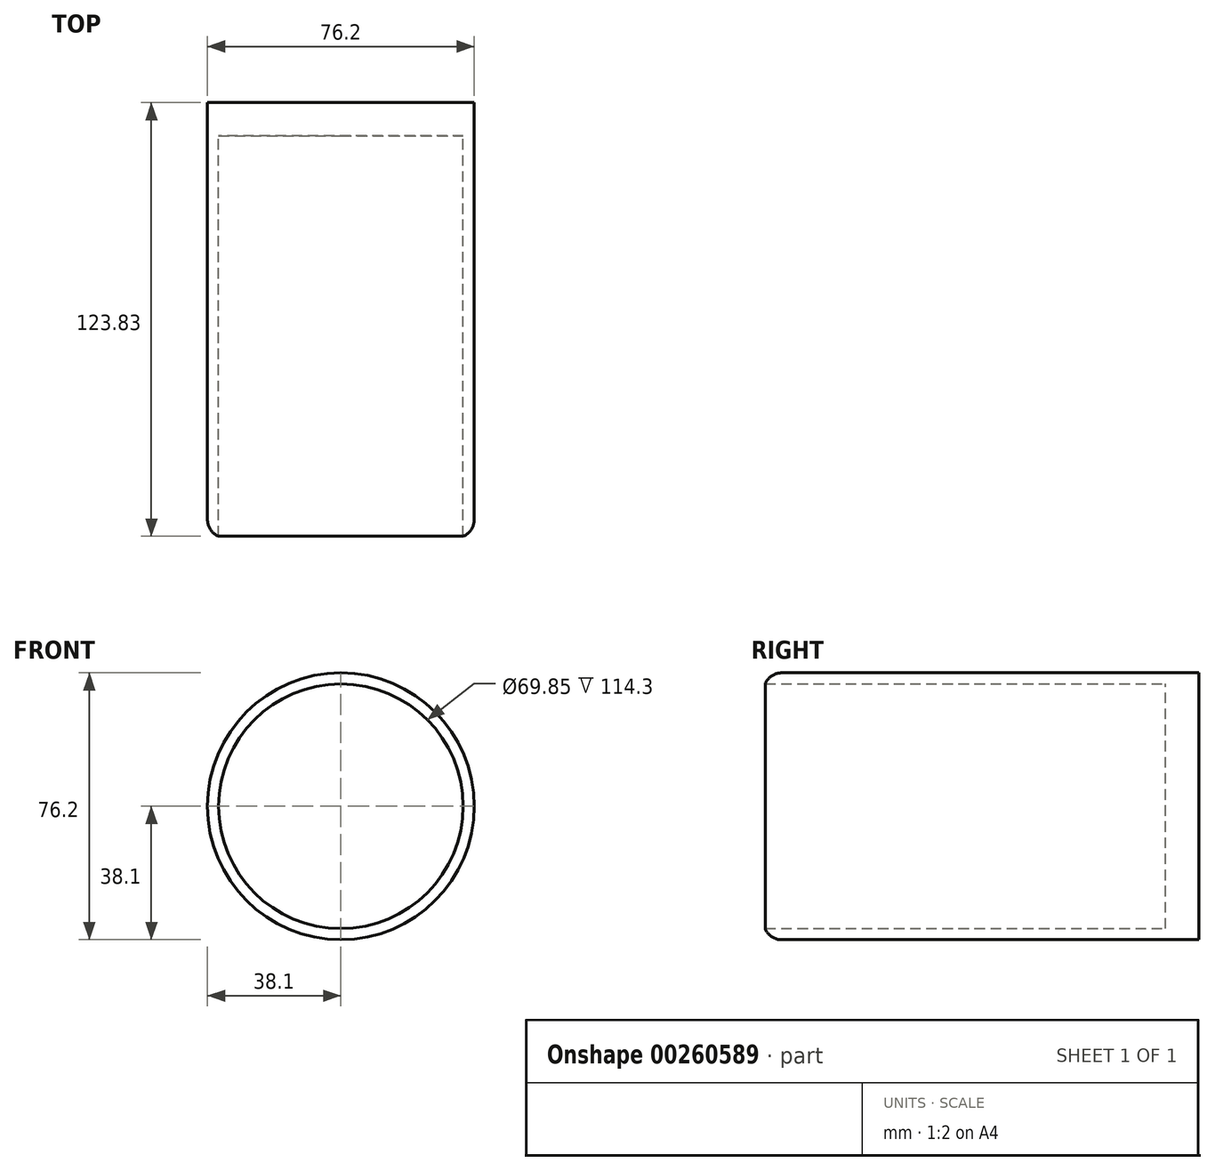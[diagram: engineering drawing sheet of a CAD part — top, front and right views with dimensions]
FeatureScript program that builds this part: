
annotation { "Feature Type Name" : "Feature", "Feature Type Description" : "" }
export const myFeature = defineFeature(function(context is Context, id is Id, definition is map)
    precondition{}
    {
        {
            var Q0;
            Q0=qCreatedBy(makeId("Front.planeOp"),FACE);
            var sketch = newSketch(context, id + "F0", { "sketchPlane" : qUnion([Q0])});
            skCircle(sketch, "E0", {"center": v(0, 0) * mm, "radius": 38.1 * mm});
            skCircle(sketch, "E1", {"center": v(0, 0) * mm, "radius": 34.93 * mm});
            skSolve(sketch);
        }
        {
            var Q0;
            Q0=makeQuery(id+"F0.imprint","IMPRINT",FACE,{"disambiguationData":[TD([[makeQuery(id+"F0.imprint","IMPRINT",EDGE,{"derivedFrom":sQuery(id+"F0.wireOp",EDGE,"E0")}),1.0]])]});
            extrude(context, id + "F1", {"entities" : qUnion([Q0]), "depth" : 123.82 * mm});
        }
        {
            var Q0;
            Q0=qCreatedBy(makeId("Front.planeOp"),FACE);
            var sketch = newSketch(context, id + "F2", { "sketchPlane" : qUnion([Q0])});
            skCircle(sketch, "E2", {"center": v(0, 0) * mm, "radius": 34.93 * mm});
            skSolve(sketch);
        }
        {
            var Q0;
            Q0=makeQuery(id+"F2.imprint","IMPRINT",FACE,{"disambiguationData":[TD([[makeQuery(id+"F2.imprint","IMPRINT",EDGE,{"derivedFrom":sQuery(id+"F2.wireOp",EDGE,"E2")}),1.0]])]});
            extrude(context, id + "F3", {"entities" : qUnion([Q0]), "operationType" : NewBodyOperationType.ADD, "depth" : 9.52 * mm});
        }
        {
            var Q0;
            Q0=makeQuery(id+"F1.opExtrude","CAP_EDGE",EDGE,{"disambiguationData":[OSD([sQuery(id+"F0.wireOp",EDGE,"E0")])],"isStart":false});
            fillet(context, id + "F4", {"entities" : qUnion([Q0]), "radius" : 5.08 * mm, "tangentPropagation" : true, "allowEdgeOverflow" : false});
        }
    });
